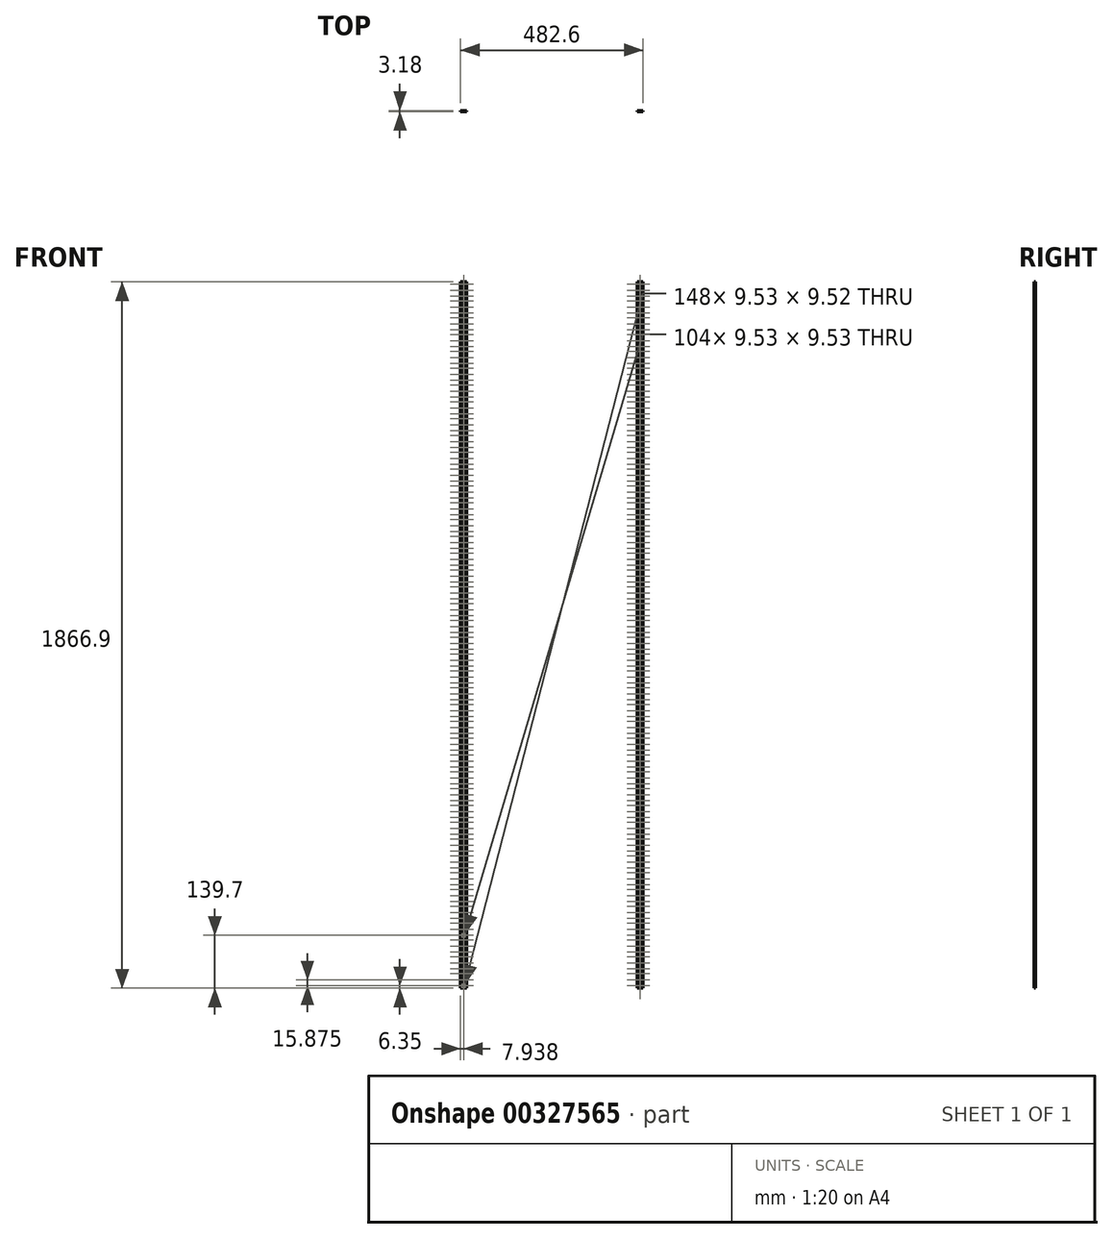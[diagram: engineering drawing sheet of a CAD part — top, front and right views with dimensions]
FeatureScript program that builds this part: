
annotation { "Feature Type Name" : "Feature", "Feature Type Description" : "" }
export const myFeature = defineFeature(function(context is Context, id is Id, definition is map)
    precondition{}
    {
        {
            var Q0;
            Q0=qCreatedBy(makeId("Front.planeOp"),FACE);
            var sketch = newSketch(context, id + "F0", { "sketchPlane" : qUnion([Q0])});
            skLineSegment(sketch, "E0.bottom", {"start": v(-241.3, 933.45) * mm, "end": v(-225.43, 933.45) * mm});
            skLineSegment(sketch, "E0.top", {"start": v(-241.3, -933.45) * mm, "end": v(-225.43, -933.45) * mm});
            skLineSegment(sketch, "E0.left", {"start": v(-241.3, 933.45) * mm, "end": v(-241.3, -933.45) * mm});
            skLineSegment(sketch, "E0.right", {"start": v(-225.43, 933.45) * mm, "end": v(-225.42, -933.45) * mm});
            skPoint(sketch, "E1", {"position": v(-241.3, 0) * mm});
            skLineSegment(sketch, "E2", {"start": v(-241.3, 0) * mm, "end": v(0, 0) * mm});
            skSolve(sketch);
        }
        {
            var Q0;
            Q0=qCreatedBy(makeId("Front.planeOp"),FACE);
            var sketch = newSketch(context, id + "F1", { "sketchPlane" : qUnion([Q0])});
            skLineSegment(sketch, "E3.bottom", {"start": v(-228.6, 1.59) * mm, "end": v(-238.13, 1.59) * mm});
            skLineSegment(sketch, "E3.top", {"start": v(-228.6, 11.11) * mm, "end": v(-238.13, 11.11) * mm});
            skLineSegment(sketch, "E3.left", {"start": v(-228.6, 1.59) * mm, "end": v(-228.6, 11.11) * mm});
            skLineSegment(sketch, "E3.right", {"start": v(-238.13, 1.59) * mm, "end": v(-238.13, 11.11) * mm});
            skPoint(sketch, "E3.middle", {"position": v(-233.36, 6.35) * mm});
            skLineSegment(sketch, "E4", {"start": v(-241.3, 0) * mm, "end": v(-225.43, 0) * mm});
            skLineSegment(sketch, "E5", {"start": v(-233.36, 0) * mm, "end": v(-233.36, 74.96) * mm});
            skPoint(sketch, "E6.0.1.0", {"position": v(-233.36, 22.22) * mm});
            skLineSegment(sketch, "E6.0.1.1", {"start": v(-228.6, 26.99) * mm, "end": v(-238.13, 26.99) * mm});
            skLineSegment(sketch, "E6.0.1.2", {"start": v(-238.12, 17.46) * mm, "end": v(-238.12, 26.99) * mm});
            skLineSegment(sketch, "E6.0.1.3", {"start": v(-228.6, 17.46) * mm, "end": v(-238.13, 17.46) * mm});
            skLineSegment(sketch, "E6.0.1.4", {"start": v(-228.6, 17.46) * mm, "end": v(-228.6, 26.99) * mm});
            skPoint(sketch, "E6.0.2.0", {"position": v(-233.36, 38.1) * mm});
            skLineSegment(sketch, "E6.0.2.1", {"start": v(-228.6, 42.86) * mm, "end": v(-238.13, 42.86) * mm});
            skLineSegment(sketch, "E6.0.2.2", {"start": v(-238.12, 33.34) * mm, "end": v(-238.12, 42.86) * mm});
            skLineSegment(sketch, "E6.0.2.3", {"start": v(-228.6, 33.34) * mm, "end": v(-238.13, 33.34) * mm});
            skLineSegment(sketch, "E6.0.2.4", {"start": v(-228.6, 33.34) * mm, "end": v(-228.6, 42.86) * mm});
            skLineSegment(sketch, "E6.direction1", {"start": v(-233.36, 6.35) * mm, "end": v(-207.96, 6.35) * mm, "construction": true});
            skLineSegment(sketch, "E6.direction2", {"start": v(-233.36, 6.35) * mm, "end": v(-233.36, 22.22) * mm, "construction": true});
            skLineSegment(sketch, "E7.MirrorCS", {"start": v(-233.36, -6.35) * mm, "end": v(-207.96, -6.35) * mm, "construction": true});
            skLineSegment(sketch, "E8.MirrorCS", {"start": v(-228.6, -11.11) * mm, "end": v(-238.13, -11.11) * mm});
            skLineSegment(sketch, "E9.MirrorCS", {"start": v(-228.6, -1.59) * mm, "end": v(-238.13, -1.59) * mm});
            skLineSegment(sketch, "E10.MirrorCS", {"start": v(-233.36, -6.35) * mm, "end": v(-233.36, -22.22) * mm, "construction": true});
            skLineSegment(sketch, "E11.MirrorCS", {"start": v(-228.6, -1.59) * mm, "end": v(-228.6, -11.11) * mm});
            skLineSegment(sketch, "E12.MirrorCS", {"start": v(-238.12, -1.59) * mm, "end": v(-238.12, -11.11) * mm});
            skLineSegment(sketch, "E13.MirrorCS", {"start": v(-238.12, -17.46) * mm, "end": v(-238.12, -26.99) * mm});
            skLineSegment(sketch, "E14.MirrorCS", {"start": v(-228.6, -26.99) * mm, "end": v(-238.13, -26.99) * mm});
            skLineSegment(sketch, "E15.MirrorCS", {"start": v(-228.6, -17.46) * mm, "end": v(-228.6, -26.99) * mm});
            skLineSegment(sketch, "E16.MirrorCS", {"start": v(-228.6, -17.46) * mm, "end": v(-238.13, -17.46) * mm});
            skLineSegment(sketch, "E17.MirrorCS", {"start": v(-228.6, -33.34) * mm, "end": v(-228.6, -42.86) * mm});
            skLineSegment(sketch, "E18.MirrorCS", {"start": v(-228.6, -42.86) * mm, "end": v(-238.13, -42.86) * mm});
            skLineSegment(sketch, "E19.MirrorCS", {"start": v(-238.12, -33.34) * mm, "end": v(-238.12, -42.86) * mm});
            skLineSegment(sketch, "E20.MirrorCS", {"start": v(-228.6, -33.34) * mm, "end": v(-238.13, -33.34) * mm});
            skLineSegment(sketch, "E21", {"start": v(-233.36, 6.35) * mm, "end": v(-233.36, -6.35) * mm});
            skLineSegment(sketch, "E22.0.1.0", {"start": v(-238.12, 61.91) * mm, "end": v(-238.12, 71.44) * mm});
            skLineSegment(sketch, "E22.0.1.1", {"start": v(-228.6, 55.56) * mm, "end": v(-238.13, 55.56) * mm});
            skLineSegment(sketch, "E22.0.1.2", {"start": v(-238.12, 77.79) * mm, "end": v(-238.12, 87.31) * mm});
            skLineSegment(sketch, "E22.0.1.3", {"start": v(-228.6, 77.79) * mm, "end": v(-228.6, 87.31) * mm});
            skLineSegment(sketch, "E22.0.1.4", {"start": v(-228.6, 46.04) * mm, "end": v(-228.6, 55.56) * mm});
            skLineSegment(sketch, "E22.0.1.5", {"start": v(-228.6, 61.91) * mm, "end": v(-238.13, 61.91) * mm});
            skLineSegment(sketch, "E22.0.1.6", {"start": v(-228.6, 46.04) * mm, "end": v(-238.13, 46.04) * mm});
            skLineSegment(sketch, "E22.0.1.7", {"start": v(-228.6, 77.79) * mm, "end": v(-238.13, 77.79) * mm});
            skLineSegment(sketch, "E22.0.1.8", {"start": v(-228.6, 71.44) * mm, "end": v(-238.13, 71.44) * mm});
            skLineSegment(sketch, "E22.0.1.9", {"start": v(-238.13, 46.04) * mm, "end": v(-238.13, 55.56) * mm});
            skLineSegment(sketch, "E22.0.1.10", {"start": v(-228.6, 61.91) * mm, "end": v(-228.6, 71.44) * mm});
            skLineSegment(sketch, "E22.0.1.11", {"start": v(-228.6, 87.31) * mm, "end": v(-238.13, 87.31) * mm});
            skLineSegment(sketch, "E22.0.2.0", {"start": v(-238.12, 106.36) * mm, "end": v(-238.12, 115.89) * mm});
            skLineSegment(sketch, "E22.0.2.1", {"start": v(-228.6, 100.01) * mm, "end": v(-238.13, 100.01) * mm});
            skLineSegment(sketch, "E22.0.2.2", {"start": v(-238.12, 122.24) * mm, "end": v(-238.12, 131.76) * mm});
            skLineSegment(sketch, "E22.0.2.3", {"start": v(-228.6, 122.24) * mm, "end": v(-228.6, 131.76) * mm});
            skLineSegment(sketch, "E22.0.2.4", {"start": v(-228.6, 90.49) * mm, "end": v(-228.6, 100.01) * mm});
            skLineSegment(sketch, "E22.0.2.5", {"start": v(-228.6, 106.36) * mm, "end": v(-238.13, 106.36) * mm});
            skLineSegment(sketch, "E22.0.2.6", {"start": v(-228.6, 90.49) * mm, "end": v(-238.13, 90.49) * mm});
            skLineSegment(sketch, "E22.0.2.7", {"start": v(-228.6, 122.24) * mm, "end": v(-238.13, 122.24) * mm});
            skLineSegment(sketch, "E22.0.2.8", {"start": v(-228.6, 115.89) * mm, "end": v(-238.13, 115.89) * mm});
            skLineSegment(sketch, "E22.0.2.9", {"start": v(-238.13, 90.49) * mm, "end": v(-238.13, 100.01) * mm});
            skLineSegment(sketch, "E22.0.2.10", {"start": v(-228.6, 106.36) * mm, "end": v(-228.6, 115.89) * mm});
            skLineSegment(sketch, "E22.0.2.11", {"start": v(-228.6, 131.76) * mm, "end": v(-238.13, 131.76) * mm});
            skLineSegment(sketch, "E22.0.3.0", {"start": v(-238.12, 150.81) * mm, "end": v(-238.12, 160.34) * mm});
            skLineSegment(sketch, "E22.0.3.1", {"start": v(-228.6, 144.46) * mm, "end": v(-238.13, 144.46) * mm});
            skLineSegment(sketch, "E22.0.3.2", {"start": v(-238.12, 166.69) * mm, "end": v(-238.12, 176.21) * mm});
            skLineSegment(sketch, "E22.0.3.3", {"start": v(-228.6, 166.69) * mm, "end": v(-228.6, 176.21) * mm});
            skLineSegment(sketch, "E22.0.3.4", {"start": v(-228.6, 134.94) * mm, "end": v(-228.6, 144.46) * mm});
            skLineSegment(sketch, "E22.0.3.5", {"start": v(-228.6, 150.81) * mm, "end": v(-238.13, 150.81) * mm});
            skLineSegment(sketch, "E22.0.3.6", {"start": v(-228.6, 134.94) * mm, "end": v(-238.13, 134.94) * mm});
            skLineSegment(sketch, "E22.0.3.7", {"start": v(-228.6, 166.69) * mm, "end": v(-238.13, 166.69) * mm});
            skLineSegment(sketch, "E22.0.3.8", {"start": v(-228.6, 160.34) * mm, "end": v(-238.13, 160.34) * mm});
            skLineSegment(sketch, "E22.0.3.9", {"start": v(-238.13, 134.94) * mm, "end": v(-238.13, 144.46) * mm});
            skLineSegment(sketch, "E22.0.3.10", {"start": v(-228.6, 150.81) * mm, "end": v(-228.6, 160.34) * mm});
            skLineSegment(sketch, "E22.0.3.11", {"start": v(-228.6, 176.21) * mm, "end": v(-238.13, 176.21) * mm});
            skLineSegment(sketch, "E22.0.4.0", {"start": v(-238.12, 195.26) * mm, "end": v(-238.12, 204.79) * mm});
            skLineSegment(sketch, "E22.0.4.1", {"start": v(-228.6, 188.91) * mm, "end": v(-238.13, 188.91) * mm});
            skLineSegment(sketch, "E22.0.4.2", {"start": v(-238.12, 211.14) * mm, "end": v(-238.12, 220.66) * mm});
            skLineSegment(sketch, "E22.0.4.3", {"start": v(-228.6, 211.14) * mm, "end": v(-228.6, 220.66) * mm});
            skLineSegment(sketch, "E22.0.4.4", {"start": v(-228.6, 179.39) * mm, "end": v(-228.6, 188.91) * mm});
            skLineSegment(sketch, "E22.0.4.5", {"start": v(-228.6, 195.26) * mm, "end": v(-238.13, 195.26) * mm});
            skLineSegment(sketch, "E22.0.4.6", {"start": v(-228.6, 179.39) * mm, "end": v(-238.13, 179.39) * mm});
            skLineSegment(sketch, "E22.0.4.7", {"start": v(-228.6, 211.14) * mm, "end": v(-238.13, 211.14) * mm});
            skLineSegment(sketch, "E22.0.4.8", {"start": v(-228.6, 204.79) * mm, "end": v(-238.13, 204.79) * mm});
            skLineSegment(sketch, "E22.0.4.9", {"start": v(-238.13, 179.39) * mm, "end": v(-238.13, 188.91) * mm});
            skLineSegment(sketch, "E22.0.4.10", {"start": v(-228.6, 195.26) * mm, "end": v(-228.6, 204.79) * mm});
            skLineSegment(sketch, "E22.0.4.11", {"start": v(-228.6, 220.66) * mm, "end": v(-238.13, 220.66) * mm});
            skLineSegment(sketch, "E22.0.5.0", {"start": v(-238.12, 239.71) * mm, "end": v(-238.12, 249.24) * mm});
            skLineSegment(sketch, "E22.0.5.1", {"start": v(-228.6, 233.36) * mm, "end": v(-238.13, 233.36) * mm});
            skLineSegment(sketch, "E22.0.5.2", {"start": v(-238.12, 255.59) * mm, "end": v(-238.12, 265.11) * mm});
            skLineSegment(sketch, "E22.0.5.3", {"start": v(-228.6, 255.59) * mm, "end": v(-228.6, 265.11) * mm});
            skLineSegment(sketch, "E22.0.5.4", {"start": v(-228.6, 223.84) * mm, "end": v(-228.6, 233.36) * mm});
            skLineSegment(sketch, "E22.0.5.5", {"start": v(-228.6, 239.71) * mm, "end": v(-238.13, 239.71) * mm});
            skLineSegment(sketch, "E22.0.5.6", {"start": v(-228.6, 223.84) * mm, "end": v(-238.13, 223.84) * mm});
            skLineSegment(sketch, "E22.0.5.7", {"start": v(-228.6, 255.59) * mm, "end": v(-238.13, 255.59) * mm});
            skLineSegment(sketch, "E22.0.5.8", {"start": v(-228.6, 249.24) * mm, "end": v(-238.13, 249.24) * mm});
            skLineSegment(sketch, "E22.0.5.9", {"start": v(-238.13, 223.84) * mm, "end": v(-238.13, 233.36) * mm});
            skLineSegment(sketch, "E22.0.5.10", {"start": v(-228.6, 239.71) * mm, "end": v(-228.6, 249.24) * mm});
            skLineSegment(sketch, "E22.0.5.11", {"start": v(-228.6, 265.11) * mm, "end": v(-238.13, 265.11) * mm});
            skLineSegment(sketch, "E22.0.6.0", {"start": v(-238.12, 284.16) * mm, "end": v(-238.12, 293.69) * mm});
            skLineSegment(sketch, "E22.0.6.1", {"start": v(-228.6, 277.81) * mm, "end": v(-238.13, 277.81) * mm});
            skLineSegment(sketch, "E22.0.6.2", {"start": v(-238.12, 300.04) * mm, "end": v(-238.12, 309.56) * mm});
            skLineSegment(sketch, "E22.0.6.3", {"start": v(-228.6, 300.04) * mm, "end": v(-228.6, 309.56) * mm});
            skLineSegment(sketch, "E22.0.6.4", {"start": v(-228.6, 268.29) * mm, "end": v(-228.6, 277.81) * mm});
            skLineSegment(sketch, "E22.0.6.5", {"start": v(-228.6, 284.16) * mm, "end": v(-238.13, 284.16) * mm});
            skLineSegment(sketch, "E22.0.6.6", {"start": v(-228.6, 268.29) * mm, "end": v(-238.13, 268.29) * mm});
            skLineSegment(sketch, "E22.0.6.7", {"start": v(-228.6, 300.04) * mm, "end": v(-238.13, 300.04) * mm});
            skLineSegment(sketch, "E22.0.6.8", {"start": v(-228.6, 293.69) * mm, "end": v(-238.13, 293.69) * mm});
            skLineSegment(sketch, "E22.0.6.9", {"start": v(-238.13, 268.29) * mm, "end": v(-238.13, 277.81) * mm});
            skLineSegment(sketch, "E22.0.6.10", {"start": v(-228.6, 284.16) * mm, "end": v(-228.6, 293.69) * mm});
            skLineSegment(sketch, "E22.0.6.11", {"start": v(-228.6, 309.56) * mm, "end": v(-238.13, 309.56) * mm});
            skLineSegment(sketch, "E22.0.7.0", {"start": v(-238.12, 328.61) * mm, "end": v(-238.12, 338.14) * mm});
            skLineSegment(sketch, "E22.0.7.1", {"start": v(-228.6, 322.26) * mm, "end": v(-238.13, 322.26) * mm});
            skLineSegment(sketch, "E22.0.7.2", {"start": v(-238.12, 344.49) * mm, "end": v(-238.12, 354.01) * mm});
            skLineSegment(sketch, "E22.0.7.3", {"start": v(-228.6, 344.49) * mm, "end": v(-228.6, 354.01) * mm});
            skLineSegment(sketch, "E22.0.7.4", {"start": v(-228.6, 312.74) * mm, "end": v(-228.6, 322.26) * mm});
            skLineSegment(sketch, "E22.0.7.5", {"start": v(-228.6, 328.61) * mm, "end": v(-238.13, 328.61) * mm});
            skLineSegment(sketch, "E22.0.7.6", {"start": v(-228.6, 312.74) * mm, "end": v(-238.13, 312.74) * mm});
            skLineSegment(sketch, "E22.0.7.7", {"start": v(-228.6, 344.49) * mm, "end": v(-238.13, 344.49) * mm});
            skLineSegment(sketch, "E22.0.7.8", {"start": v(-228.6, 338.14) * mm, "end": v(-238.13, 338.14) * mm});
            skLineSegment(sketch, "E22.0.7.9", {"start": v(-238.13, 312.74) * mm, "end": v(-238.13, 322.26) * mm});
            skLineSegment(sketch, "E22.0.7.10", {"start": v(-228.6, 328.61) * mm, "end": v(-228.6, 338.14) * mm});
            skLineSegment(sketch, "E22.0.7.11", {"start": v(-228.6, 354.01) * mm, "end": v(-238.13, 354.01) * mm});
            skLineSegment(sketch, "E22.0.8.0", {"start": v(-238.12, 373.06) * mm, "end": v(-238.12, 382.59) * mm});
            skLineSegment(sketch, "E22.0.8.1", {"start": v(-228.6, 366.71) * mm, "end": v(-238.13, 366.71) * mm});
            skLineSegment(sketch, "E22.0.8.2", {"start": v(-238.12, 388.94) * mm, "end": v(-238.12, 398.46) * mm});
            skLineSegment(sketch, "E22.0.8.3", {"start": v(-228.6, 388.94) * mm, "end": v(-228.6, 398.46) * mm});
            skLineSegment(sketch, "E22.0.8.4", {"start": v(-228.6, 357.19) * mm, "end": v(-228.6, 366.71) * mm});
            skLineSegment(sketch, "E22.0.8.5", {"start": v(-228.6, 373.06) * mm, "end": v(-238.13, 373.06) * mm});
            skLineSegment(sketch, "E22.0.8.6", {"start": v(-228.6, 357.19) * mm, "end": v(-238.13, 357.19) * mm});
            skLineSegment(sketch, "E22.0.8.7", {"start": v(-228.6, 388.94) * mm, "end": v(-238.13, 388.94) * mm});
            skLineSegment(sketch, "E22.0.8.8", {"start": v(-228.6, 382.59) * mm, "end": v(-238.13, 382.59) * mm});
            skLineSegment(sketch, "E22.0.8.9", {"start": v(-238.13, 357.19) * mm, "end": v(-238.13, 366.71) * mm});
            skLineSegment(sketch, "E22.0.8.10", {"start": v(-228.6, 373.06) * mm, "end": v(-228.6, 382.59) * mm});
            skLineSegment(sketch, "E22.0.8.11", {"start": v(-228.6, 398.46) * mm, "end": v(-238.13, 398.46) * mm});
            skLineSegment(sketch, "E22.0.9.0", {"start": v(-238.12, 417.51) * mm, "end": v(-238.12, 427.04) * mm});
            skLineSegment(sketch, "E22.0.9.1", {"start": v(-228.6, 411.16) * mm, "end": v(-238.13, 411.16) * mm});
            skLineSegment(sketch, "E22.0.9.2", {"start": v(-238.12, 433.39) * mm, "end": v(-238.12, 442.91) * mm});
            skLineSegment(sketch, "E22.0.9.3", {"start": v(-228.6, 433.39) * mm, "end": v(-228.6, 442.91) * mm});
            skLineSegment(sketch, "E22.0.9.4", {"start": v(-228.6, 401.64) * mm, "end": v(-228.6, 411.16) * mm});
            skLineSegment(sketch, "E22.0.9.5", {"start": v(-228.6, 417.51) * mm, "end": v(-238.13, 417.51) * mm});
            skLineSegment(sketch, "E22.0.9.6", {"start": v(-228.6, 401.64) * mm, "end": v(-238.13, 401.64) * mm});
            skLineSegment(sketch, "E22.0.9.7", {"start": v(-228.6, 433.39) * mm, "end": v(-238.13, 433.39) * mm});
            skLineSegment(sketch, "E22.0.9.8", {"start": v(-228.6, 427.04) * mm, "end": v(-238.13, 427.04) * mm});
            skLineSegment(sketch, "E22.0.9.9", {"start": v(-238.13, 401.64) * mm, "end": v(-238.13, 411.16) * mm});
            skLineSegment(sketch, "E22.0.9.10", {"start": v(-228.6, 417.51) * mm, "end": v(-228.6, 427.04) * mm});
            skLineSegment(sketch, "E22.0.9.11", {"start": v(-228.6, 442.91) * mm, "end": v(-238.13, 442.91) * mm});
            skLineSegment(sketch, "E22.0.10.0", {"start": v(-238.12, 461.96) * mm, "end": v(-238.12, 471.49) * mm});
            skLineSegment(sketch, "E22.0.10.1", {"start": v(-228.6, 455.61) * mm, "end": v(-238.13, 455.61) * mm});
            skLineSegment(sketch, "E22.0.10.2", {"start": v(-238.12, 477.84) * mm, "end": v(-238.12, 487.36) * mm});
            skLineSegment(sketch, "E22.0.10.3", {"start": v(-228.6, 477.84) * mm, "end": v(-228.6, 487.36) * mm});
            skLineSegment(sketch, "E22.0.10.4", {"start": v(-228.6, 446.09) * mm, "end": v(-228.6, 455.61) * mm});
            skLineSegment(sketch, "E22.0.10.5", {"start": v(-228.6, 461.96) * mm, "end": v(-238.13, 461.96) * mm});
            skLineSegment(sketch, "E22.0.10.6", {"start": v(-228.6, 446.09) * mm, "end": v(-238.13, 446.09) * mm});
            skLineSegment(sketch, "E22.0.10.7", {"start": v(-228.6, 477.84) * mm, "end": v(-238.13, 477.84) * mm});
            skLineSegment(sketch, "E22.0.10.8", {"start": v(-228.6, 471.49) * mm, "end": v(-238.13, 471.49) * mm});
            skLineSegment(sketch, "E22.0.10.9", {"start": v(-238.13, 446.09) * mm, "end": v(-238.13, 455.61) * mm});
            skLineSegment(sketch, "E22.0.10.10", {"start": v(-228.6, 461.96) * mm, "end": v(-228.6, 471.49) * mm});
            skLineSegment(sketch, "E22.0.10.11", {"start": v(-228.6, 487.36) * mm, "end": v(-238.13, 487.36) * mm});
            skLineSegment(sketch, "E22.0.11.0", {"start": v(-238.12, 506.41) * mm, "end": v(-238.12, 515.94) * mm});
            skLineSegment(sketch, "E22.0.11.1", {"start": v(-228.6, 500.06) * mm, "end": v(-238.13, 500.06) * mm});
            skLineSegment(sketch, "E22.0.11.2", {"start": v(-238.12, 522.29) * mm, "end": v(-238.12, 531.81) * mm});
            skLineSegment(sketch, "E22.0.11.3", {"start": v(-228.6, 522.29) * mm, "end": v(-228.6, 531.81) * mm});
            skLineSegment(sketch, "E22.0.11.4", {"start": v(-228.6, 490.54) * mm, "end": v(-228.6, 500.06) * mm});
            skLineSegment(sketch, "E22.0.11.5", {"start": v(-228.6, 506.41) * mm, "end": v(-238.13, 506.41) * mm});
            skLineSegment(sketch, "E22.0.11.6", {"start": v(-228.6, 490.54) * mm, "end": v(-238.13, 490.54) * mm});
            skLineSegment(sketch, "E22.0.11.7", {"start": v(-228.6, 522.29) * mm, "end": v(-238.13, 522.29) * mm});
            skLineSegment(sketch, "E22.0.11.8", {"start": v(-228.6, 515.94) * mm, "end": v(-238.13, 515.94) * mm});
            skLineSegment(sketch, "E22.0.11.9", {"start": v(-238.13, 490.54) * mm, "end": v(-238.13, 500.06) * mm});
            skLineSegment(sketch, "E22.0.11.10", {"start": v(-228.6, 506.41) * mm, "end": v(-228.6, 515.94) * mm});
            skLineSegment(sketch, "E22.0.11.11", {"start": v(-228.6, 531.81) * mm, "end": v(-238.13, 531.81) * mm});
            skLineSegment(sketch, "E22.0.12.0", {"start": v(-238.12, 550.86) * mm, "end": v(-238.12, 560.39) * mm});
            skLineSegment(sketch, "E22.0.12.1", {"start": v(-228.6, 544.51) * mm, "end": v(-238.13, 544.51) * mm});
            skLineSegment(sketch, "E22.0.12.2", {"start": v(-238.12, 566.74) * mm, "end": v(-238.12, 576.26) * mm});
            skLineSegment(sketch, "E22.0.12.3", {"start": v(-228.6, 566.74) * mm, "end": v(-228.6, 576.26) * mm});
            skLineSegment(sketch, "E22.0.12.4", {"start": v(-228.6, 534.99) * mm, "end": v(-228.6, 544.51) * mm});
            skLineSegment(sketch, "E22.0.12.5", {"start": v(-228.6, 550.86) * mm, "end": v(-238.13, 550.86) * mm});
            skLineSegment(sketch, "E22.0.12.6", {"start": v(-228.6, 534.99) * mm, "end": v(-238.13, 534.99) * mm});
            skLineSegment(sketch, "E22.0.12.7", {"start": v(-228.6, 566.74) * mm, "end": v(-238.13, 566.74) * mm});
            skLineSegment(sketch, "E22.0.12.8", {"start": v(-228.6, 560.39) * mm, "end": v(-238.13, 560.39) * mm});
            skLineSegment(sketch, "E22.0.12.9", {"start": v(-238.13, 534.99) * mm, "end": v(-238.13, 544.51) * mm});
            skLineSegment(sketch, "E22.0.12.10", {"start": v(-228.6, 550.86) * mm, "end": v(-228.6, 560.39) * mm});
            skLineSegment(sketch, "E22.0.12.11", {"start": v(-228.6, 576.26) * mm, "end": v(-238.13, 576.26) * mm});
            skLineSegment(sketch, "E22.0.13.0", {"start": v(-238.12, 595.31) * mm, "end": v(-238.12, 604.84) * mm});
            skLineSegment(sketch, "E22.0.13.1", {"start": v(-228.6, 588.96) * mm, "end": v(-238.13, 588.96) * mm});
            skLineSegment(sketch, "E22.0.13.2", {"start": v(-238.12, 611.19) * mm, "end": v(-238.12, 620.71) * mm});
            skLineSegment(sketch, "E22.0.13.3", {"start": v(-228.6, 611.19) * mm, "end": v(-228.6, 620.71) * mm});
            skLineSegment(sketch, "E22.0.13.4", {"start": v(-228.6, 579.44) * mm, "end": v(-228.6, 588.96) * mm});
            skLineSegment(sketch, "E22.0.13.5", {"start": v(-228.6, 595.31) * mm, "end": v(-238.13, 595.31) * mm});
            skLineSegment(sketch, "E22.0.13.6", {"start": v(-228.6, 579.44) * mm, "end": v(-238.13, 579.44) * mm});
            skLineSegment(sketch, "E22.0.13.7", {"start": v(-228.6, 611.19) * mm, "end": v(-238.13, 611.19) * mm});
            skLineSegment(sketch, "E22.0.13.8", {"start": v(-228.6, 604.84) * mm, "end": v(-238.13, 604.84) * mm});
            skLineSegment(sketch, "E22.0.13.9", {"start": v(-238.13, 579.44) * mm, "end": v(-238.13, 588.96) * mm});
            skLineSegment(sketch, "E22.0.13.10", {"start": v(-228.6, 595.31) * mm, "end": v(-228.6, 604.84) * mm});
            skLineSegment(sketch, "E22.0.13.11", {"start": v(-228.6, 620.71) * mm, "end": v(-238.13, 620.71) * mm});
            skLineSegment(sketch, "E22.0.14.0", {"start": v(-238.12, 639.76) * mm, "end": v(-238.12, 649.29) * mm});
            skLineSegment(sketch, "E22.0.14.1", {"start": v(-228.6, 633.41) * mm, "end": v(-238.13, 633.41) * mm});
            skLineSegment(sketch, "E22.0.14.2", {"start": v(-238.12, 655.64) * mm, "end": v(-238.12, 665.16) * mm});
            skLineSegment(sketch, "E22.0.14.3", {"start": v(-228.6, 655.64) * mm, "end": v(-228.6, 665.16) * mm});
            skLineSegment(sketch, "E22.0.14.4", {"start": v(-228.6, 623.89) * mm, "end": v(-228.6, 633.41) * mm});
            skLineSegment(sketch, "E22.0.14.5", {"start": v(-228.6, 639.76) * mm, "end": v(-238.13, 639.76) * mm});
            skLineSegment(sketch, "E22.0.14.6", {"start": v(-228.6, 623.89) * mm, "end": v(-238.13, 623.89) * mm});
            skLineSegment(sketch, "E22.0.14.7", {"start": v(-228.6, 655.64) * mm, "end": v(-238.13, 655.64) * mm});
            skLineSegment(sketch, "E22.0.14.8", {"start": v(-228.6, 649.29) * mm, "end": v(-238.13, 649.29) * mm});
            skLineSegment(sketch, "E22.0.14.9", {"start": v(-238.13, 623.89) * mm, "end": v(-238.13, 633.41) * mm});
            skLineSegment(sketch, "E22.0.14.10", {"start": v(-228.6, 639.76) * mm, "end": v(-228.6, 649.29) * mm});
            skLineSegment(sketch, "E22.0.14.11", {"start": v(-228.6, 665.16) * mm, "end": v(-238.13, 665.16) * mm});
            skLineSegment(sketch, "E22.0.15.0", {"start": v(-238.12, 684.21) * mm, "end": v(-238.12, 693.74) * mm});
            skLineSegment(sketch, "E22.0.15.1", {"start": v(-228.6, 677.86) * mm, "end": v(-238.13, 677.86) * mm});
            skLineSegment(sketch, "E22.0.15.2", {"start": v(-238.12, 700.09) * mm, "end": v(-238.12, 709.61) * mm});
            skLineSegment(sketch, "E22.0.15.3", {"start": v(-228.6, 700.09) * mm, "end": v(-228.6, 709.61) * mm});
            skLineSegment(sketch, "E22.0.15.4", {"start": v(-228.6, 668.34) * mm, "end": v(-228.6, 677.86) * mm});
            skLineSegment(sketch, "E22.0.15.5", {"start": v(-228.6, 684.21) * mm, "end": v(-238.13, 684.21) * mm});
            skLineSegment(sketch, "E22.0.15.6", {"start": v(-228.6, 668.34) * mm, "end": v(-238.13, 668.34) * mm});
            skLineSegment(sketch, "E22.0.15.7", {"start": v(-228.6, 700.09) * mm, "end": v(-238.13, 700.09) * mm});
            skLineSegment(sketch, "E22.0.15.8", {"start": v(-228.6, 693.74) * mm, "end": v(-238.13, 693.74) * mm});
            skLineSegment(sketch, "E22.0.15.9", {"start": v(-238.13, 668.34) * mm, "end": v(-238.13, 677.86) * mm});
            skLineSegment(sketch, "E22.0.15.10", {"start": v(-228.6, 684.21) * mm, "end": v(-228.6, 693.74) * mm});
            skLineSegment(sketch, "E22.0.15.11", {"start": v(-228.6, 709.61) * mm, "end": v(-238.13, 709.61) * mm});
            skLineSegment(sketch, "E22.0.16.0", {"start": v(-238.12, 728.66) * mm, "end": v(-238.12, 738.19) * mm});
            skLineSegment(sketch, "E22.0.16.1", {"start": v(-228.6, 722.31) * mm, "end": v(-238.13, 722.31) * mm});
            skLineSegment(sketch, "E22.0.16.2", {"start": v(-238.12, 744.54) * mm, "end": v(-238.12, 754.06) * mm});
            skLineSegment(sketch, "E22.0.16.3", {"start": v(-228.6, 744.54) * mm, "end": v(-228.6, 754.06) * mm});
            skLineSegment(sketch, "E22.0.16.4", {"start": v(-228.6, 712.79) * mm, "end": v(-228.6, 722.31) * mm});
            skLineSegment(sketch, "E22.0.16.5", {"start": v(-228.6, 728.66) * mm, "end": v(-238.13, 728.66) * mm});
            skLineSegment(sketch, "E22.0.16.6", {"start": v(-228.6, 712.79) * mm, "end": v(-238.13, 712.79) * mm});
            skLineSegment(sketch, "E22.0.16.7", {"start": v(-228.6, 744.54) * mm, "end": v(-238.13, 744.54) * mm});
            skLineSegment(sketch, "E22.0.16.8", {"start": v(-228.6, 738.19) * mm, "end": v(-238.13, 738.19) * mm});
            skLineSegment(sketch, "E22.0.16.9", {"start": v(-238.13, 712.79) * mm, "end": v(-238.13, 722.31) * mm});
            skLineSegment(sketch, "E22.0.16.10", {"start": v(-228.6, 728.66) * mm, "end": v(-228.6, 738.19) * mm});
            skLineSegment(sketch, "E22.0.16.11", {"start": v(-228.6, 754.06) * mm, "end": v(-238.13, 754.06) * mm});
            skLineSegment(sketch, "E22.0.17.0", {"start": v(-238.12, 773.11) * mm, "end": v(-238.12, 782.64) * mm});
            skLineSegment(sketch, "E22.0.17.1", {"start": v(-228.6, 766.76) * mm, "end": v(-238.13, 766.76) * mm});
            skLineSegment(sketch, "E22.0.17.2", {"start": v(-238.12, 788.99) * mm, "end": v(-238.12, 798.51) * mm});
            skLineSegment(sketch, "E22.0.17.3", {"start": v(-228.6, 788.99) * mm, "end": v(-228.6, 798.51) * mm});
            skLineSegment(sketch, "E22.0.17.4", {"start": v(-228.6, 757.24) * mm, "end": v(-228.6, 766.76) * mm});
            skLineSegment(sketch, "E22.0.17.5", {"start": v(-228.6, 773.11) * mm, "end": v(-238.13, 773.11) * mm});
            skLineSegment(sketch, "E22.0.17.6", {"start": v(-228.6, 757.24) * mm, "end": v(-238.13, 757.24) * mm});
            skLineSegment(sketch, "E22.0.17.7", {"start": v(-228.6, 788.99) * mm, "end": v(-238.13, 788.99) * mm});
            skLineSegment(sketch, "E22.0.17.8", {"start": v(-228.6, 782.64) * mm, "end": v(-238.13, 782.64) * mm});
            skLineSegment(sketch, "E22.0.17.9", {"start": v(-238.13, 757.24) * mm, "end": v(-238.13, 766.76) * mm});
            skLineSegment(sketch, "E22.0.17.10", {"start": v(-228.6, 773.11) * mm, "end": v(-228.6, 782.64) * mm});
            skLineSegment(sketch, "E22.0.17.11", {"start": v(-228.6, 798.51) * mm, "end": v(-238.13, 798.51) * mm});
            skLineSegment(sketch, "E22.0.18.0", {"start": v(-238.12, 817.56) * mm, "end": v(-238.12, 827.09) * mm});
            skLineSegment(sketch, "E22.0.18.1", {"start": v(-228.6, 811.21) * mm, "end": v(-238.13, 811.21) * mm});
            skLineSegment(sketch, "E22.0.18.2", {"start": v(-238.12, 833.44) * mm, "end": v(-238.12, 842.96) * mm});
            skLineSegment(sketch, "E22.0.18.3", {"start": v(-228.6, 833.44) * mm, "end": v(-228.6, 842.96) * mm});
            skLineSegment(sketch, "E22.0.18.4", {"start": v(-228.6, 801.69) * mm, "end": v(-228.6, 811.21) * mm});
            skLineSegment(sketch, "E22.0.18.5", {"start": v(-228.6, 817.56) * mm, "end": v(-238.13, 817.56) * mm});
            skLineSegment(sketch, "E22.0.18.6", {"start": v(-228.6, 801.69) * mm, "end": v(-238.13, 801.69) * mm});
            skLineSegment(sketch, "E22.0.18.7", {"start": v(-228.6, 833.44) * mm, "end": v(-238.13, 833.44) * mm});
            skLineSegment(sketch, "E22.0.18.8", {"start": v(-228.6, 827.09) * mm, "end": v(-238.13, 827.09) * mm});
            skLineSegment(sketch, "E22.0.18.9", {"start": v(-238.13, 801.69) * mm, "end": v(-238.13, 811.21) * mm});
            skLineSegment(sketch, "E22.0.18.10", {"start": v(-228.6, 817.56) * mm, "end": v(-228.6, 827.09) * mm});
            skLineSegment(sketch, "E22.0.18.11", {"start": v(-228.6, 842.96) * mm, "end": v(-238.13, 842.96) * mm});
            skLineSegment(sketch, "E22.0.19.0", {"start": v(-238.12, 862.01) * mm, "end": v(-238.12, 871.54) * mm});
            skLineSegment(sketch, "E22.0.19.1", {"start": v(-228.6, 855.66) * mm, "end": v(-238.13, 855.66) * mm});
            skLineSegment(sketch, "E22.0.19.2", {"start": v(-238.12, 877.89) * mm, "end": v(-238.12, 887.41) * mm});
            skLineSegment(sketch, "E22.0.19.3", {"start": v(-228.6, 877.89) * mm, "end": v(-228.6, 887.41) * mm});
            skLineSegment(sketch, "E22.0.19.4", {"start": v(-228.6, 846.14) * mm, "end": v(-228.6, 855.66) * mm});
            skLineSegment(sketch, "E22.0.19.5", {"start": v(-228.6, 862.01) * mm, "end": v(-238.13, 862.01) * mm});
            skLineSegment(sketch, "E22.0.19.6", {"start": v(-228.6, 846.14) * mm, "end": v(-238.13, 846.14) * mm});
            skLineSegment(sketch, "E22.0.19.7", {"start": v(-228.6, 877.89) * mm, "end": v(-238.13, 877.89) * mm});
            skLineSegment(sketch, "E22.0.19.8", {"start": v(-228.6, 871.54) * mm, "end": v(-238.13, 871.54) * mm});
            skLineSegment(sketch, "E22.0.19.9", {"start": v(-238.13, 846.14) * mm, "end": v(-238.13, 855.66) * mm});
            skLineSegment(sketch, "E22.0.19.10", {"start": v(-228.6, 862.01) * mm, "end": v(-228.6, 871.54) * mm});
            skLineSegment(sketch, "E22.0.19.11", {"start": v(-228.6, 887.41) * mm, "end": v(-238.13, 887.41) * mm});
            skLineSegment(sketch, "E22.0.20.0", {"start": v(-238.12, 906.46) * mm, "end": v(-238.12, 915.99) * mm});
            skLineSegment(sketch, "E22.0.20.1", {"start": v(-228.6, 900.11) * mm, "end": v(-238.13, 900.11) * mm});
            skLineSegment(sketch, "E22.0.20.2", {"start": v(-238.12, 922.34) * mm, "end": v(-238.12, 931.86) * mm});
            skLineSegment(sketch, "E22.0.20.3", {"start": v(-228.6, 922.34) * mm, "end": v(-228.6, 931.86) * mm});
            skLineSegment(sketch, "E22.0.20.4", {"start": v(-228.6, 890.59) * mm, "end": v(-228.6, 900.11) * mm});
            skLineSegment(sketch, "E22.0.20.5", {"start": v(-228.6, 906.46) * mm, "end": v(-238.13, 906.46) * mm});
            skLineSegment(sketch, "E22.0.20.6", {"start": v(-228.6, 890.59) * mm, "end": v(-238.13, 890.59) * mm});
            skLineSegment(sketch, "E22.0.20.7", {"start": v(-228.6, 922.34) * mm, "end": v(-238.13, 922.34) * mm});
            skLineSegment(sketch, "E22.0.20.8", {"start": v(-228.6, 915.99) * mm, "end": v(-238.13, 915.99) * mm});
            skLineSegment(sketch, "E22.0.20.9", {"start": v(-238.13, 890.59) * mm, "end": v(-238.13, 900.11) * mm});
            skLineSegment(sketch, "E22.0.20.10", {"start": v(-228.6, 906.46) * mm, "end": v(-228.6, 915.99) * mm});
            skLineSegment(sketch, "E22.0.20.11", {"start": v(-228.6, 931.86) * mm, "end": v(-238.13, 931.86) * mm});
            skLineSegment(sketch, "E22.direction1", {"start": v(-238.13, 1.59) * mm, "end": v(-212.73, 1.59) * mm, "construction": true});
            skLineSegment(sketch, "E22.direction2", {"start": v(-238.13, 1.59) * mm, "end": v(-238.13, 46.04) * mm, "construction": true});
            skLineSegment(sketch, "E23.0.1.0", {"start": v(-228.6, -55.56) * mm, "end": v(-238.13, -55.56) * mm});
            skLineSegment(sketch, "E23.0.1.1", {"start": v(-228.6, -46.04) * mm, "end": v(-228.6, -55.56) * mm});
            skLineSegment(sketch, "E23.0.1.2", {"start": v(-228.6, -46.04) * mm, "end": v(-238.13, -46.04) * mm});
            skLineSegment(sketch, "E23.0.1.3", {"start": v(-238.12, -46.04) * mm, "end": v(-238.12, -55.56) * mm});
            skLineSegment(sketch, "E23.0.1.4", {"start": v(-228.6, -61.91) * mm, "end": v(-238.13, -61.91) * mm});
            skLineSegment(sketch, "E23.0.1.5", {"start": v(-238.12, -61.91) * mm, "end": v(-238.12, -71.44) * mm});
            skLineSegment(sketch, "E23.0.1.6", {"start": v(-228.6, -61.91) * mm, "end": v(-228.6, -71.44) * mm});
            skLineSegment(sketch, "E23.0.1.7", {"start": v(-228.6, -71.44) * mm, "end": v(-238.13, -71.44) * mm});
            skLineSegment(sketch, "E23.0.1.8", {"start": v(-228.6, -77.79) * mm, "end": v(-228.6, -87.31) * mm});
            skLineSegment(sketch, "E23.0.1.9", {"start": v(-238.12, -77.79) * mm, "end": v(-238.12, -87.31) * mm});
            skLineSegment(sketch, "E23.0.1.10", {"start": v(-228.6, -77.79) * mm, "end": v(-238.13, -77.79) * mm});
            skLineSegment(sketch, "E23.0.1.11", {"start": v(-228.6, -87.31) * mm, "end": v(-238.13, -87.31) * mm});
            skLineSegment(sketch, "E23.0.2.0", {"start": v(-228.6, -100.01) * mm, "end": v(-238.13, -100.01) * mm});
            skLineSegment(sketch, "E23.0.2.1", {"start": v(-228.6, -90.49) * mm, "end": v(-228.6, -100.01) * mm});
            skLineSegment(sketch, "E23.0.2.2", {"start": v(-228.6, -90.49) * mm, "end": v(-238.13, -90.49) * mm});
            skLineSegment(sketch, "E23.0.2.3", {"start": v(-238.12, -90.49) * mm, "end": v(-238.12, -100.01) * mm});
            skLineSegment(sketch, "E23.0.2.4", {"start": v(-228.6, -106.36) * mm, "end": v(-238.13, -106.36) * mm});
            skLineSegment(sketch, "E23.0.2.5", {"start": v(-238.12, -106.36) * mm, "end": v(-238.12, -115.89) * mm});
            skLineSegment(sketch, "E23.0.2.6", {"start": v(-228.6, -106.36) * mm, "end": v(-228.6, -115.89) * mm});
            skLineSegment(sketch, "E23.0.2.7", {"start": v(-228.6, -115.89) * mm, "end": v(-238.13, -115.89) * mm});
            skLineSegment(sketch, "E23.0.2.8", {"start": v(-228.6, -122.24) * mm, "end": v(-228.6, -131.76) * mm});
            skLineSegment(sketch, "E23.0.2.9", {"start": v(-238.12, -122.24) * mm, "end": v(-238.12, -131.76) * mm});
            skLineSegment(sketch, "E23.0.2.10", {"start": v(-228.6, -122.24) * mm, "end": v(-238.13, -122.24) * mm});
            skLineSegment(sketch, "E23.0.2.11", {"start": v(-228.6, -131.76) * mm, "end": v(-238.13, -131.76) * mm});
            skLineSegment(sketch, "E23.0.3.0", {"start": v(-228.6, -144.46) * mm, "end": v(-238.13, -144.46) * mm});
            skLineSegment(sketch, "E23.0.3.1", {"start": v(-228.6, -134.94) * mm, "end": v(-228.6, -144.46) * mm});
            skLineSegment(sketch, "E23.0.3.2", {"start": v(-228.6, -134.94) * mm, "end": v(-238.13, -134.94) * mm});
            skLineSegment(sketch, "E23.0.3.3", {"start": v(-238.12, -134.94) * mm, "end": v(-238.12, -144.46) * mm});
            skLineSegment(sketch, "E23.0.3.4", {"start": v(-228.6, -150.81) * mm, "end": v(-238.13, -150.81) * mm});
            skLineSegment(sketch, "E23.0.3.5", {"start": v(-238.12, -150.81) * mm, "end": v(-238.12, -160.34) * mm});
            skLineSegment(sketch, "E23.0.3.6", {"start": v(-228.6, -150.81) * mm, "end": v(-228.6, -160.34) * mm});
            skLineSegment(sketch, "E23.0.3.7", {"start": v(-228.6, -160.34) * mm, "end": v(-238.13, -160.34) * mm});
            skLineSegment(sketch, "E23.0.3.8", {"start": v(-228.6, -166.69) * mm, "end": v(-228.6, -176.21) * mm});
            skLineSegment(sketch, "E23.0.3.9", {"start": v(-238.12, -166.69) * mm, "end": v(-238.12, -176.21) * mm});
            skLineSegment(sketch, "E23.0.3.10", {"start": v(-228.6, -166.69) * mm, "end": v(-238.13, -166.69) * mm});
            skLineSegment(sketch, "E23.0.3.11", {"start": v(-228.6, -176.21) * mm, "end": v(-238.13, -176.21) * mm});
            skLineSegment(sketch, "E23.0.4.0", {"start": v(-228.6, -188.91) * mm, "end": v(-238.13, -188.91) * mm});
            skLineSegment(sketch, "E23.0.4.1", {"start": v(-228.6, -179.39) * mm, "end": v(-228.6, -188.91) * mm});
            skLineSegment(sketch, "E23.0.4.2", {"start": v(-228.6, -179.39) * mm, "end": v(-238.13, -179.39) * mm});
            skLineSegment(sketch, "E23.0.4.3", {"start": v(-238.12, -179.39) * mm, "end": v(-238.12, -188.91) * mm});
            skLineSegment(sketch, "E23.0.4.4", {"start": v(-228.6, -195.26) * mm, "end": v(-238.13, -195.26) * mm});
            skLineSegment(sketch, "E23.0.4.5", {"start": v(-238.12, -195.26) * mm, "end": v(-238.12, -204.79) * mm});
            skLineSegment(sketch, "E23.0.4.6", {"start": v(-228.6, -195.26) * mm, "end": v(-228.6, -204.79) * mm});
            skLineSegment(sketch, "E23.0.4.7", {"start": v(-228.6, -204.79) * mm, "end": v(-238.13, -204.79) * mm});
            skLineSegment(sketch, "E23.0.4.8", {"start": v(-228.6, -211.14) * mm, "end": v(-228.6, -220.66) * mm});
            skLineSegment(sketch, "E23.0.4.9", {"start": v(-238.12, -211.14) * mm, "end": v(-238.12, -220.66) * mm});
            skLineSegment(sketch, "E23.0.4.10", {"start": v(-228.6, -211.14) * mm, "end": v(-238.13, -211.14) * mm});
            skLineSegment(sketch, "E23.0.4.11", {"start": v(-228.6, -220.66) * mm, "end": v(-238.13, -220.66) * mm});
            skLineSegment(sketch, "E23.0.5.0", {"start": v(-228.6, -233.36) * mm, "end": v(-238.13, -233.36) * mm});
            skLineSegment(sketch, "E23.0.5.1", {"start": v(-228.6, -223.84) * mm, "end": v(-228.6, -233.36) * mm});
            skLineSegment(sketch, "E23.0.5.2", {"start": v(-228.6, -223.84) * mm, "end": v(-238.13, -223.84) * mm});
            skLineSegment(sketch, "E23.0.5.3", {"start": v(-238.12, -223.84) * mm, "end": v(-238.12, -233.36) * mm});
            skLineSegment(sketch, "E23.0.5.4", {"start": v(-228.6, -239.71) * mm, "end": v(-238.13, -239.71) * mm});
            skLineSegment(sketch, "E23.0.5.5", {"start": v(-238.12, -239.71) * mm, "end": v(-238.12, -249.24) * mm});
            skLineSegment(sketch, "E23.0.5.6", {"start": v(-228.6, -239.71) * mm, "end": v(-228.6, -249.24) * mm});
            skLineSegment(sketch, "E23.0.5.7", {"start": v(-228.6, -249.24) * mm, "end": v(-238.13, -249.24) * mm});
            skLineSegment(sketch, "E23.0.5.8", {"start": v(-228.6, -255.59) * mm, "end": v(-228.6, -265.11) * mm});
            skLineSegment(sketch, "E23.0.5.9", {"start": v(-238.12, -255.59) * mm, "end": v(-238.12, -265.11) * mm});
            skLineSegment(sketch, "E23.0.5.10", {"start": v(-228.6, -255.59) * mm, "end": v(-238.13, -255.59) * mm});
            skLineSegment(sketch, "E23.0.5.11", {"start": v(-228.6, -265.11) * mm, "end": v(-238.13, -265.11) * mm});
            skLineSegment(sketch, "E23.0.6.0", {"start": v(-228.6, -277.81) * mm, "end": v(-238.13, -277.81) * mm});
            skLineSegment(sketch, "E23.0.6.1", {"start": v(-228.6, -268.29) * mm, "end": v(-228.6, -277.81) * mm});
            skLineSegment(sketch, "E23.0.6.2", {"start": v(-228.6, -268.29) * mm, "end": v(-238.13, -268.29) * mm});
            skLineSegment(sketch, "E23.0.6.3", {"start": v(-238.12, -268.29) * mm, "end": v(-238.12, -277.81) * mm});
            skLineSegment(sketch, "E23.0.6.4", {"start": v(-228.6, -284.16) * mm, "end": v(-238.13, -284.16) * mm});
            skLineSegment(sketch, "E23.0.6.5", {"start": v(-238.12, -284.16) * mm, "end": v(-238.12, -293.69) * mm});
            skLineSegment(sketch, "E23.0.6.6", {"start": v(-228.6, -284.16) * mm, "end": v(-228.6, -293.69) * mm});
            skLineSegment(sketch, "E23.0.6.7", {"start": v(-228.6, -293.69) * mm, "end": v(-238.13, -293.69) * mm});
            skLineSegment(sketch, "E23.0.6.8", {"start": v(-228.6, -300.04) * mm, "end": v(-228.6, -309.56) * mm});
            skLineSegment(sketch, "E23.0.6.9", {"start": v(-238.12, -300.04) * mm, "end": v(-238.12, -309.56) * mm});
            skLineSegment(sketch, "E23.0.6.10", {"start": v(-228.6, -300.04) * mm, "end": v(-238.13, -300.04) * mm});
            skLineSegment(sketch, "E23.0.6.11", {"start": v(-228.6, -309.56) * mm, "end": v(-238.13, -309.56) * mm});
            skLineSegment(sketch, "E23.0.7.0", {"start": v(-228.6, -322.26) * mm, "end": v(-238.13, -322.26) * mm});
            skLineSegment(sketch, "E23.0.7.1", {"start": v(-228.6, -312.74) * mm, "end": v(-228.6, -322.26) * mm});
            skLineSegment(sketch, "E23.0.7.2", {"start": v(-228.6, -312.74) * mm, "end": v(-238.13, -312.74) * mm});
            skLineSegment(sketch, "E23.0.7.3", {"start": v(-238.12, -312.74) * mm, "end": v(-238.12, -322.26) * mm});
            skLineSegment(sketch, "E23.0.7.4", {"start": v(-228.6, -328.61) * mm, "end": v(-238.13, -328.61) * mm});
            skLineSegment(sketch, "E23.0.7.5", {"start": v(-238.12, -328.61) * mm, "end": v(-238.12, -338.14) * mm});
            skLineSegment(sketch, "E23.0.7.6", {"start": v(-228.6, -328.61) * mm, "end": v(-228.6, -338.14) * mm});
            skLineSegment(sketch, "E23.0.7.7", {"start": v(-228.6, -338.14) * mm, "end": v(-238.13, -338.14) * mm});
            skLineSegment(sketch, "E23.0.7.8", {"start": v(-228.6, -344.49) * mm, "end": v(-228.6, -354.01) * mm});
            skLineSegment(sketch, "E23.0.7.9", {"start": v(-238.12, -344.49) * mm, "end": v(-238.12, -354.01) * mm});
            skLineSegment(sketch, "E23.0.7.10", {"start": v(-228.6, -344.49) * mm, "end": v(-238.13, -344.49) * mm});
            skLineSegment(sketch, "E23.0.7.11", {"start": v(-228.6, -354.01) * mm, "end": v(-238.13, -354.01) * mm});
            skLineSegment(sketch, "E23.0.8.0", {"start": v(-228.6, -366.71) * mm, "end": v(-238.13, -366.71) * mm});
            skLineSegment(sketch, "E23.0.8.1", {"start": v(-228.6, -357.19) * mm, "end": v(-228.6, -366.71) * mm});
            skLineSegment(sketch, "E23.0.8.2", {"start": v(-228.6, -357.19) * mm, "end": v(-238.13, -357.19) * mm});
            skLineSegment(sketch, "E23.0.8.3", {"start": v(-238.12, -357.19) * mm, "end": v(-238.12, -366.71) * mm});
            skLineSegment(sketch, "E23.0.8.4", {"start": v(-228.6, -373.06) * mm, "end": v(-238.13, -373.06) * mm});
            skLineSegment(sketch, "E23.0.8.5", {"start": v(-238.12, -373.06) * mm, "end": v(-238.12, -382.59) * mm});
            skLineSegment(sketch, "E23.0.8.6", {"start": v(-228.6, -373.06) * mm, "end": v(-228.6, -382.59) * mm});
            skLineSegment(sketch, "E23.0.8.7", {"start": v(-228.6, -382.59) * mm, "end": v(-238.13, -382.59) * mm});
            skLineSegment(sketch, "E23.0.8.8", {"start": v(-228.6, -388.94) * mm, "end": v(-228.6, -398.46) * mm});
            skLineSegment(sketch, "E23.0.8.9", {"start": v(-238.12, -388.94) * mm, "end": v(-238.12, -398.46) * mm});
            skLineSegment(sketch, "E23.0.8.10", {"start": v(-228.6, -388.94) * mm, "end": v(-238.13, -388.94) * mm});
            skLineSegment(sketch, "E23.0.8.11", {"start": v(-228.6, -398.46) * mm, "end": v(-238.13, -398.46) * mm});
            skLineSegment(sketch, "E23.0.9.0", {"start": v(-228.6, -411.16) * mm, "end": v(-238.13, -411.16) * mm});
            skLineSegment(sketch, "E23.0.9.1", {"start": v(-228.6, -401.64) * mm, "end": v(-228.6, -411.16) * mm});
            skLineSegment(sketch, "E23.0.9.2", {"start": v(-228.6, -401.64) * mm, "end": v(-238.13, -401.64) * mm});
            skLineSegment(sketch, "E23.0.9.3", {"start": v(-238.12, -401.64) * mm, "end": v(-238.12, -411.16) * mm});
            skLineSegment(sketch, "E23.0.9.4", {"start": v(-228.6, -417.51) * mm, "end": v(-238.13, -417.51) * mm});
            skLineSegment(sketch, "E23.0.9.5", {"start": v(-238.12, -417.51) * mm, "end": v(-238.12, -427.04) * mm});
            skLineSegment(sketch, "E23.0.9.6", {"start": v(-228.6, -417.51) * mm, "end": v(-228.6, -427.04) * mm});
            skLineSegment(sketch, "E23.0.9.7", {"start": v(-228.6, -427.04) * mm, "end": v(-238.13, -427.04) * mm});
            skLineSegment(sketch, "E23.0.9.8", {"start": v(-228.6, -433.39) * mm, "end": v(-228.6, -442.91) * mm});
            skLineSegment(sketch, "E23.0.9.9", {"start": v(-238.12, -433.39) * mm, "end": v(-238.12, -442.91) * mm});
            skLineSegment(sketch, "E23.0.9.10", {"start": v(-228.6, -433.39) * mm, "end": v(-238.13, -433.39) * mm});
            skLineSegment(sketch, "E23.0.9.11", {"start": v(-228.6, -442.91) * mm, "end": v(-238.13, -442.91) * mm});
            skLineSegment(sketch, "E23.0.10.0", {"start": v(-228.6, -455.61) * mm, "end": v(-238.13, -455.61) * mm});
            skLineSegment(sketch, "E23.0.10.1", {"start": v(-228.6, -446.09) * mm, "end": v(-228.6, -455.61) * mm});
            skLineSegment(sketch, "E23.0.10.2", {"start": v(-228.6, -446.09) * mm, "end": v(-238.13, -446.09) * mm});
            skLineSegment(sketch, "E23.0.10.3", {"start": v(-238.12, -446.09) * mm, "end": v(-238.12, -455.61) * mm});
            skLineSegment(sketch, "E23.0.10.4", {"start": v(-228.6, -461.96) * mm, "end": v(-238.13, -461.96) * mm});
            skLineSegment(sketch, "E23.0.10.5", {"start": v(-238.12, -461.96) * mm, "end": v(-238.12, -471.49) * mm});
            skLineSegment(sketch, "E23.0.10.6", {"start": v(-228.6, -461.96) * mm, "end": v(-228.6, -471.49) * mm});
            skLineSegment(sketch, "E23.0.10.7", {"start": v(-228.6, -471.49) * mm, "end": v(-238.13, -471.49) * mm});
            skLineSegment(sketch, "E23.0.10.8", {"start": v(-228.6, -477.84) * mm, "end": v(-228.6, -487.36) * mm});
            skLineSegment(sketch, "E23.0.10.9", {"start": v(-238.12, -477.84) * mm, "end": v(-238.12, -487.36) * mm});
            skLineSegment(sketch, "E23.0.10.10", {"start": v(-228.6, -477.84) * mm, "end": v(-238.13, -477.84) * mm});
            skLineSegment(sketch, "E23.0.10.11", {"start": v(-228.6, -487.36) * mm, "end": v(-238.13, -487.36) * mm});
            skLineSegment(sketch, "E23.0.11.0", {"start": v(-228.6, -500.06) * mm, "end": v(-238.13, -500.06) * mm});
            skLineSegment(sketch, "E23.0.11.1", {"start": v(-228.6, -490.54) * mm, "end": v(-228.6, -500.06) * mm});
            skLineSegment(sketch, "E23.0.11.2", {"start": v(-228.6, -490.54) * mm, "end": v(-238.13, -490.54) * mm});
            skLineSegment(sketch, "E23.0.11.3", {"start": v(-238.12, -490.54) * mm, "end": v(-238.12, -500.06) * mm});
            skLineSegment(sketch, "E23.0.11.4", {"start": v(-228.6, -506.41) * mm, "end": v(-238.13, -506.41) * mm});
            skLineSegment(sketch, "E23.0.11.5", {"start": v(-238.12, -506.41) * mm, "end": v(-238.12, -515.94) * mm});
            skLineSegment(sketch, "E23.0.11.6", {"start": v(-228.6, -506.41) * mm, "end": v(-228.6, -515.94) * mm});
            skLineSegment(sketch, "E23.0.11.7", {"start": v(-228.6, -515.94) * mm, "end": v(-238.13, -515.94) * mm});
            skLineSegment(sketch, "E23.0.11.8", {"start": v(-228.6, -522.29) * mm, "end": v(-228.6, -531.81) * mm});
            skLineSegment(sketch, "E23.0.11.9", {"start": v(-238.12, -522.29) * mm, "end": v(-238.12, -531.81) * mm});
            skLineSegment(sketch, "E23.0.11.10", {"start": v(-228.6, -522.29) * mm, "end": v(-238.13, -522.29) * mm});
            skLineSegment(sketch, "E23.0.11.11", {"start": v(-228.6, -531.81) * mm, "end": v(-238.13, -531.81) * mm});
            skLineSegment(sketch, "E23.0.12.0", {"start": v(-228.6, -544.51) * mm, "end": v(-238.13, -544.51) * mm});
            skLineSegment(sketch, "E23.0.12.1", {"start": v(-228.6, -534.99) * mm, "end": v(-228.6, -544.51) * mm});
            skLineSegment(sketch, "E23.0.12.2", {"start": v(-228.6, -534.99) * mm, "end": v(-238.13, -534.99) * mm});
            skLineSegment(sketch, "E23.0.12.3", {"start": v(-238.12, -534.99) * mm, "end": v(-238.12, -544.51) * mm});
            skLineSegment(sketch, "E23.0.12.4", {"start": v(-228.6, -550.86) * mm, "end": v(-238.13, -550.86) * mm});
            skLineSegment(sketch, "E23.0.12.5", {"start": v(-238.12, -550.86) * mm, "end": v(-238.12, -560.39) * mm});
            skLineSegment(sketch, "E23.0.12.6", {"start": v(-228.6, -550.86) * mm, "end": v(-228.6, -560.39) * mm});
            skLineSegment(sketch, "E23.0.12.7", {"start": v(-228.6, -560.39) * mm, "end": v(-238.13, -560.39) * mm});
            skLineSegment(sketch, "E23.0.12.8", {"start": v(-228.6, -566.74) * mm, "end": v(-228.6, -576.26) * mm});
            skLineSegment(sketch, "E23.0.12.9", {"start": v(-238.12, -566.74) * mm, "end": v(-238.12, -576.26) * mm});
            skLineSegment(sketch, "E23.0.12.10", {"start": v(-228.6, -566.74) * mm, "end": v(-238.13, -566.74) * mm});
            skLineSegment(sketch, "E23.0.12.11", {"start": v(-228.6, -576.26) * mm, "end": v(-238.13, -576.26) * mm});
            skLineSegment(sketch, "E23.0.13.0", {"start": v(-228.6, -588.96) * mm, "end": v(-238.13, -588.96) * mm});
            skLineSegment(sketch, "E23.0.13.1", {"start": v(-228.6, -579.44) * mm, "end": v(-228.6, -588.96) * mm});
            skLineSegment(sketch, "E23.0.13.2", {"start": v(-228.6, -579.44) * mm, "end": v(-238.13, -579.44) * mm});
            skLineSegment(sketch, "E23.0.13.3", {"start": v(-238.12, -579.44) * mm, "end": v(-238.12, -588.96) * mm});
            skLineSegment(sketch, "E23.0.13.4", {"start": v(-228.6, -595.31) * mm, "end": v(-238.13, -595.31) * mm});
            skLineSegment(sketch, "E23.0.13.5", {"start": v(-238.12, -595.31) * mm, "end": v(-238.12, -604.84) * mm});
            skLineSegment(sketch, "E23.0.13.6", {"start": v(-228.6, -595.31) * mm, "end": v(-228.6, -604.84) * mm});
            skLineSegment(sketch, "E23.0.13.7", {"start": v(-228.6, -604.84) * mm, "end": v(-238.13, -604.84) * mm});
            skLineSegment(sketch, "E23.0.13.8", {"start": v(-228.6, -611.19) * mm, "end": v(-228.6, -620.71) * mm});
            skLineSegment(sketch, "E23.0.13.9", {"start": v(-238.12, -611.19) * mm, "end": v(-238.12, -620.71) * mm});
            skLineSegment(sketch, "E23.0.13.10", {"start": v(-228.6, -611.19) * mm, "end": v(-238.13, -611.19) * mm});
            skLineSegment(sketch, "E23.0.13.11", {"start": v(-228.6, -620.71) * mm, "end": v(-238.13, -620.71) * mm});
            skLineSegment(sketch, "E23.0.14.0", {"start": v(-228.6, -633.41) * mm, "end": v(-238.13, -633.41) * mm});
            skLineSegment(sketch, "E23.0.14.1", {"start": v(-228.6, -623.89) * mm, "end": v(-228.6, -633.41) * mm});
            skLineSegment(sketch, "E23.0.14.2", {"start": v(-228.6, -623.89) * mm, "end": v(-238.13, -623.89) * mm});
            skLineSegment(sketch, "E23.0.14.3", {"start": v(-238.12, -623.89) * mm, "end": v(-238.12, -633.41) * mm});
            skLineSegment(sketch, "E23.0.14.4", {"start": v(-228.6, -639.76) * mm, "end": v(-238.13, -639.76) * mm});
            skLineSegment(sketch, "E23.0.14.5", {"start": v(-238.12, -639.76) * mm, "end": v(-238.12, -649.29) * mm});
            skLineSegment(sketch, "E23.0.14.6", {"start": v(-228.6, -639.76) * mm, "end": v(-228.6, -649.29) * mm});
            skLineSegment(sketch, "E23.0.14.7", {"start": v(-228.6, -649.29) * mm, "end": v(-238.13, -649.29) * mm});
            skLineSegment(sketch, "E23.0.14.8", {"start": v(-228.6, -655.64) * mm, "end": v(-228.6, -665.16) * mm});
            skLineSegment(sketch, "E23.0.14.9", {"start": v(-238.12, -655.64) * mm, "end": v(-238.12, -665.16) * mm});
            skLineSegment(sketch, "E23.0.14.10", {"start": v(-228.6, -655.64) * mm, "end": v(-238.13, -655.64) * mm});
            skLineSegment(sketch, "E23.0.14.11", {"start": v(-228.6, -665.16) * mm, "end": v(-238.13, -665.16) * mm});
            skLineSegment(sketch, "E23.0.15.0", {"start": v(-228.6, -677.86) * mm, "end": v(-238.13, -677.86) * mm});
            skLineSegment(sketch, "E23.0.15.1", {"start": v(-228.6, -668.34) * mm, "end": v(-228.6, -677.86) * mm});
            skLineSegment(sketch, "E23.0.15.2", {"start": v(-228.6, -668.34) * mm, "end": v(-238.13, -668.34) * mm});
            skLineSegment(sketch, "E23.0.15.3", {"start": v(-238.12, -668.34) * mm, "end": v(-238.12, -677.86) * mm});
            skLineSegment(sketch, "E23.0.15.4", {"start": v(-228.6, -684.21) * mm, "end": v(-238.13, -684.21) * mm});
            skLineSegment(sketch, "E23.0.15.5", {"start": v(-238.12, -684.21) * mm, "end": v(-238.12, -693.74) * mm});
            skLineSegment(sketch, "E23.0.15.6", {"start": v(-228.6, -684.21) * mm, "end": v(-228.6, -693.74) * mm});
            skLineSegment(sketch, "E23.0.15.7", {"start": v(-228.6, -693.74) * mm, "end": v(-238.13, -693.74) * mm});
            skLineSegment(sketch, "E23.0.15.8", {"start": v(-228.6, -700.09) * mm, "end": v(-228.6, -709.61) * mm});
            skLineSegment(sketch, "E23.0.15.9", {"start": v(-238.12, -700.09) * mm, "end": v(-238.12, -709.61) * mm});
            skLineSegment(sketch, "E23.0.15.10", {"start": v(-228.6, -700.09) * mm, "end": v(-238.13, -700.09) * mm});
            skLineSegment(sketch, "E23.0.15.11", {"start": v(-228.6, -709.61) * mm, "end": v(-238.13, -709.61) * mm});
            skLineSegment(sketch, "E23.0.16.0", {"start": v(-228.6, -722.31) * mm, "end": v(-238.13, -722.31) * mm});
            skLineSegment(sketch, "E23.0.16.1", {"start": v(-228.6, -712.79) * mm, "end": v(-228.6, -722.31) * mm});
            skLineSegment(sketch, "E23.0.16.2", {"start": v(-228.6, -712.79) * mm, "end": v(-238.13, -712.79) * mm});
            skLineSegment(sketch, "E23.0.16.3", {"start": v(-238.12, -712.79) * mm, "end": v(-238.12, -722.31) * mm});
            skLineSegment(sketch, "E23.0.16.4", {"start": v(-228.6, -728.66) * mm, "end": v(-238.13, -728.66) * mm});
            skLineSegment(sketch, "E23.0.16.5", {"start": v(-238.12, -728.66) * mm, "end": v(-238.12, -738.19) * mm});
            skLineSegment(sketch, "E23.0.16.6", {"start": v(-228.6, -728.66) * mm, "end": v(-228.6, -738.19) * mm});
            skLineSegment(sketch, "E23.0.16.7", {"start": v(-228.6, -738.19) * mm, "end": v(-238.13, -738.19) * mm});
            skLineSegment(sketch, "E23.0.16.8", {"start": v(-228.6, -744.54) * mm, "end": v(-228.6, -754.06) * mm});
            skLineSegment(sketch, "E23.0.16.9", {"start": v(-238.12, -744.54) * mm, "end": v(-238.12, -754.06) * mm});
            skLineSegment(sketch, "E23.0.16.10", {"start": v(-228.6, -744.54) * mm, "end": v(-238.13, -744.54) * mm});
            skLineSegment(sketch, "E23.0.16.11", {"start": v(-228.6, -754.06) * mm, "end": v(-238.13, -754.06) * mm});
            skLineSegment(sketch, "E23.0.17.0", {"start": v(-228.6, -766.76) * mm, "end": v(-238.13, -766.76) * mm});
            skLineSegment(sketch, "E23.0.17.1", {"start": v(-228.6, -757.24) * mm, "end": v(-228.6, -766.76) * mm});
            skLineSegment(sketch, "E23.0.17.2", {"start": v(-228.6, -757.24) * mm, "end": v(-238.13, -757.24) * mm});
            skLineSegment(sketch, "E23.0.17.3", {"start": v(-238.12, -757.24) * mm, "end": v(-238.12, -766.76) * mm});
            skLineSegment(sketch, "E23.0.17.4", {"start": v(-228.6, -773.11) * mm, "end": v(-238.13, -773.11) * mm});
            skLineSegment(sketch, "E23.0.17.5", {"start": v(-238.12, -773.11) * mm, "end": v(-238.12, -782.64) * mm});
            skLineSegment(sketch, "E23.0.17.6", {"start": v(-228.6, -773.11) * mm, "end": v(-228.6, -782.64) * mm});
            skLineSegment(sketch, "E23.0.17.7", {"start": v(-228.6, -782.64) * mm, "end": v(-238.13, -782.64) * mm});
            skLineSegment(sketch, "E23.0.17.8", {"start": v(-228.6, -788.99) * mm, "end": v(-228.6, -798.51) * mm});
            skLineSegment(sketch, "E23.0.17.9", {"start": v(-238.12, -788.99) * mm, "end": v(-238.12, -798.51) * mm});
            skLineSegment(sketch, "E23.0.17.10", {"start": v(-228.6, -788.99) * mm, "end": v(-238.13, -788.99) * mm});
            skLineSegment(sketch, "E23.0.17.11", {"start": v(-228.6, -798.51) * mm, "end": v(-238.13, -798.51) * mm});
            skLineSegment(sketch, "E23.0.18.0", {"start": v(-228.6, -811.21) * mm, "end": v(-238.13, -811.21) * mm});
            skLineSegment(sketch, "E23.0.18.1", {"start": v(-228.6, -801.69) * mm, "end": v(-228.6, -811.21) * mm});
            skLineSegment(sketch, "E23.0.18.2", {"start": v(-228.6, -801.69) * mm, "end": v(-238.13, -801.69) * mm});
            skLineSegment(sketch, "E23.0.18.3", {"start": v(-238.12, -801.69) * mm, "end": v(-238.12, -811.21) * mm});
            skLineSegment(sketch, "E23.0.18.4", {"start": v(-228.6, -817.56) * mm, "end": v(-238.13, -817.56) * mm});
            skLineSegment(sketch, "E23.0.18.5", {"start": v(-238.12, -817.56) * mm, "end": v(-238.12, -827.09) * mm});
            skLineSegment(sketch, "E23.0.18.6", {"start": v(-228.6, -817.56) * mm, "end": v(-228.6, -827.09) * mm});
            skLineSegment(sketch, "E23.0.18.7", {"start": v(-228.6, -827.09) * mm, "end": v(-238.13, -827.09) * mm});
            skLineSegment(sketch, "E23.0.18.8", {"start": v(-228.6, -833.44) * mm, "end": v(-228.6, -842.96) * mm});
            skLineSegment(sketch, "E23.0.18.9", {"start": v(-238.12, -833.44) * mm, "end": v(-238.12, -842.96) * mm});
            skLineSegment(sketch, "E23.0.18.10", {"start": v(-228.6, -833.44) * mm, "end": v(-238.13, -833.44) * mm});
            skLineSegment(sketch, "E23.0.18.11", {"start": v(-228.6, -842.96) * mm, "end": v(-238.13, -842.96) * mm});
            skLineSegment(sketch, "E23.0.19.0", {"start": v(-228.6, -855.66) * mm, "end": v(-238.13, -855.66) * mm});
            skLineSegment(sketch, "E23.0.19.1", {"start": v(-228.6, -846.14) * mm, "end": v(-228.6, -855.66) * mm});
            skLineSegment(sketch, "E23.0.19.2", {"start": v(-228.6, -846.14) * mm, "end": v(-238.13, -846.14) * mm});
            skLineSegment(sketch, "E23.0.19.3", {"start": v(-238.12, -846.14) * mm, "end": v(-238.12, -855.66) * mm});
            skLineSegment(sketch, "E23.0.19.4", {"start": v(-228.6, -862.01) * mm, "end": v(-238.13, -862.01) * mm});
            skLineSegment(sketch, "E23.0.19.5", {"start": v(-238.12, -862.01) * mm, "end": v(-238.12, -871.54) * mm});
            skLineSegment(sketch, "E23.0.19.6", {"start": v(-228.6, -862.01) * mm, "end": v(-228.6, -871.54) * mm});
            skLineSegment(sketch, "E23.0.19.7", {"start": v(-228.6, -871.54) * mm, "end": v(-238.13, -871.54) * mm});
            skLineSegment(sketch, "E23.0.19.8", {"start": v(-228.6, -877.89) * mm, "end": v(-228.6, -887.41) * mm});
            skLineSegment(sketch, "E23.0.19.9", {"start": v(-238.12, -877.89) * mm, "end": v(-238.12, -887.41) * mm});
            skLineSegment(sketch, "E23.0.19.10", {"start": v(-228.6, -877.89) * mm, "end": v(-238.13, -877.89) * mm});
            skLineSegment(sketch, "E23.0.19.11", {"start": v(-228.6, -887.41) * mm, "end": v(-238.13, -887.41) * mm});
            skLineSegment(sketch, "E23.0.20.0", {"start": v(-228.6, -900.11) * mm, "end": v(-238.13, -900.11) * mm});
            skLineSegment(sketch, "E23.0.20.1", {"start": v(-228.6, -890.59) * mm, "end": v(-228.6, -900.11) * mm});
            skLineSegment(sketch, "E23.0.20.2", {"start": v(-228.6, -890.59) * mm, "end": v(-238.13, -890.59) * mm});
            skLineSegment(sketch, "E23.0.20.3", {"start": v(-238.12, -890.59) * mm, "end": v(-238.12, -900.11) * mm});
            skLineSegment(sketch, "E23.0.20.4", {"start": v(-228.6, -906.46) * mm, "end": v(-238.13, -906.46) * mm});
            skLineSegment(sketch, "E23.0.20.5", {"start": v(-238.12, -906.46) * mm, "end": v(-238.12, -915.99) * mm});
            skLineSegment(sketch, "E23.0.20.6", {"start": v(-228.6, -906.46) * mm, "end": v(-228.6, -915.99) * mm});
            skLineSegment(sketch, "E23.0.20.7", {"start": v(-228.6, -915.99) * mm, "end": v(-238.13, -915.99) * mm});
            skLineSegment(sketch, "E23.0.20.8", {"start": v(-228.6, -922.34) * mm, "end": v(-228.6, -931.86) * mm});
            skLineSegment(sketch, "E23.0.20.9", {"start": v(-238.12, -922.34) * mm, "end": v(-238.12, -931.86) * mm});
            skLineSegment(sketch, "E23.0.20.10", {"start": v(-228.6, -922.34) * mm, "end": v(-238.13, -922.34) * mm});
            skLineSegment(sketch, "E23.0.20.11", {"start": v(-228.6, -931.86) * mm, "end": v(-238.13, -931.86) * mm});
            skLineSegment(sketch, "E23.direction1", {"start": v(-238.13, -11.11) * mm, "end": v(-212.73, -11.11) * mm, "construction": true});
            skLineSegment(sketch, "E23.direction2", {"start": v(-238.13, -11.11) * mm, "end": v(-238.13, -55.56) * mm, "construction": true});
            skSolve(sketch);
        }
        {
            var Q0;
            {var subQ0=sQuery(id+"F0.wireOp",EDGE,"E0.bottom");Q0=makeQuery(id+"F0.imprint","IMPRINT",FACE,{"disambiguationData":[TD([[makeQuery(id+"F0.imprint","IMPRINT",EDGE,{"derivedFrom":subQ0}),-1.0]])]});}
            var Q1;
            {var subQ0=sQuery(id+"F0.wireOp",EDGE,"E0.top");Q1=makeQuery(id+"F0.imprint","IMPRINT",FACE,{"disambiguationData":[TD([[makeQuery(id+"F0.imprint","IMPRINT",EDGE,{"derivedFrom":subQ0}),1.0]])]});}
            extrude(context, id + "F2", {"entities" : qUnion([Q0, Q1]), "oppositeDirection" : true, "depth" : 3.17 * mm});
        }
        {
            var Q0;
            Q0 = qSketchRegion(id + "F1", true);
            extrude(context, id + "F3", {"entities" : qUnion([Q0]), "operationType" : NewBodyOperationType.REMOVE, "endBound" : BoundingType.SYMMETRIC, "oppositeDirection" : true, "depth" : 25.4 * mm});
        }
        {
            var Q0;
            Q0=makeQuery(id+"F2.opExtrude","SWEPT_BODY",BODY,{"disambiguationData":[OSD([sQuery(id+"F0.wireOp",EDGE,"E0.bottom"),sQuery(id+"F0.wireOp",EDGE,"E0.top"),sQuery(id+"F0.wireOp",EDGE,"E0.left"),sQuery(id+"F0.wireOp",EDGE,"E0.right")])]});
            var Q1;
            Q1=qCreatedBy(makeId("Right.planeOp"),FACE);
            mirror(context, id + "F4", {"entities" : qUnion([Q0]), "mirrorPlane" : qUnion([Q1])});
        }
    });
